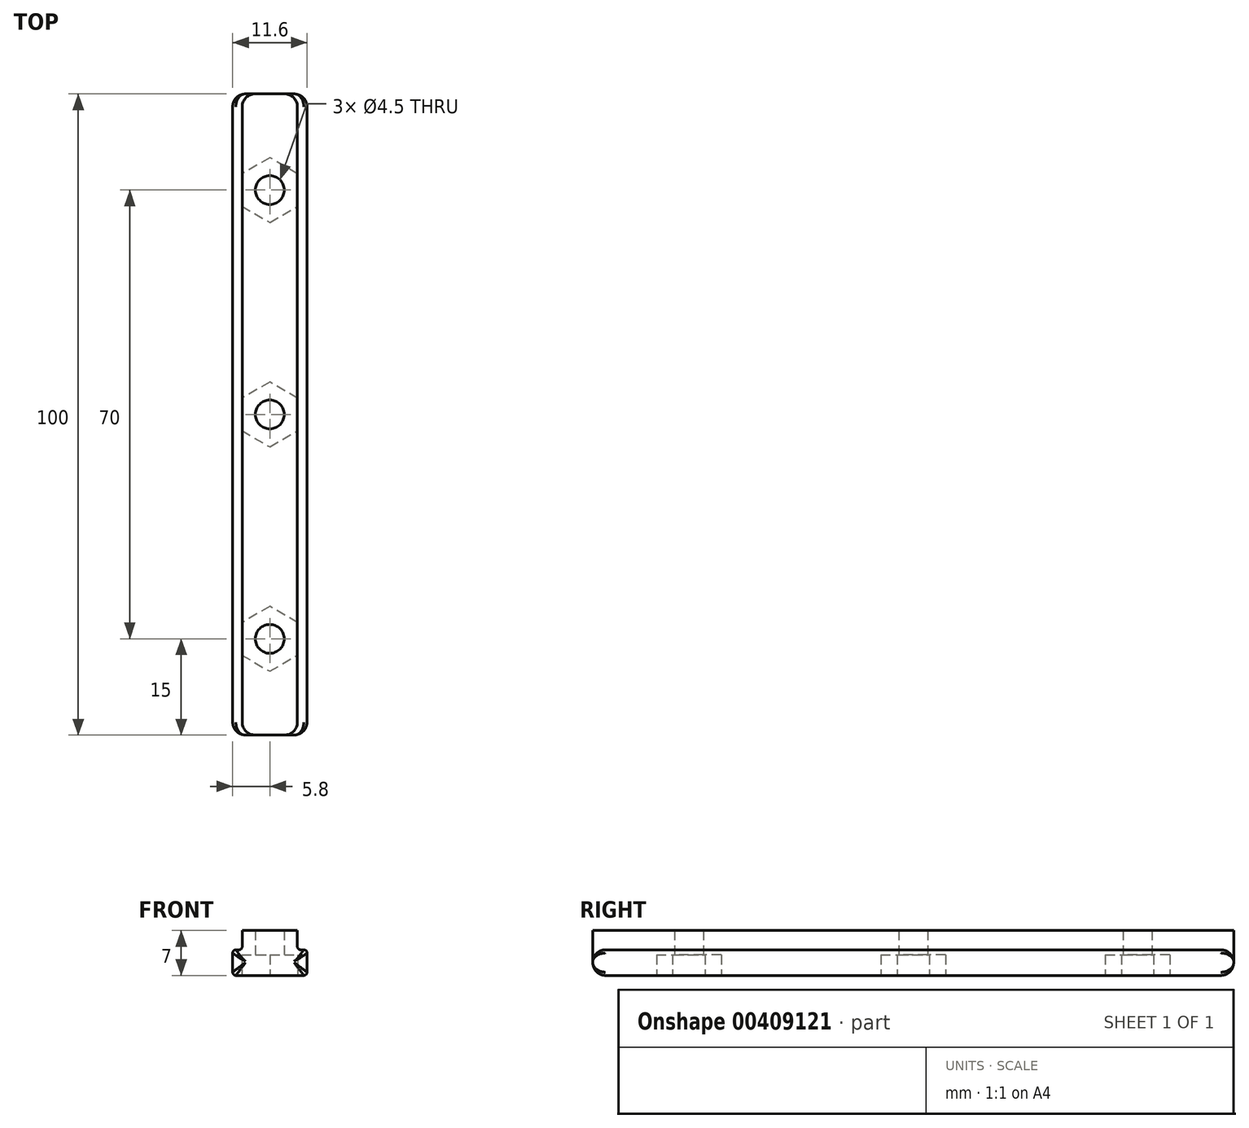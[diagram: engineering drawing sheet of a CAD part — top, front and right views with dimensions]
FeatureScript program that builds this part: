
annotation { "Feature Type Name" : "Feature", "Feature Type Description" : "" }
export const myFeature = defineFeature(function(context is Context, id is Id, definition is map)
    precondition{}
    {
        {
            var Q0;
            Q0=qCreatedBy(makeId("Front.planeOp"),FACE);
            var sketch = newSketch(context, id + "F0", { "sketchPlane" : qUnion([Q0])});
            skLineSegment(sketch, "E0", {"start": v(0, 0) * mm, "end": v(5.8, 0) * mm});
            skLineSegment(sketch, "E1", {"start": v(5.8, 0) * mm, "end": v(5.8, 4) * mm});
            skLineSegment(sketch, "E2", {"start": v(5.8, 4) * mm, "end": v(4.3, 4) * mm});
            skLineSegment(sketch, "E3", {"start": v(4.3, 4) * mm, "end": v(4.3, 7) * mm});
            skLineSegment(sketch, "E4", {"start": v(4.3, 7) * mm, "end": v(0, 7) * mm});
            skLineSegment(sketch, "E5", {"start": v(0, 0) * mm, "end": v(-5.8, 0) * mm});
            skLineSegment(sketch, "E6", {"start": v(-5.8, 0) * mm, "end": v(-5.8, 4) * mm});
            skLineSegment(sketch, "E7", {"start": v(-5.8, 4) * mm, "end": v(-4.3, 4) * mm});
            skLineSegment(sketch, "E8", {"start": v(-4.3, 4) * mm, "end": v(-4.3, 7) * mm});
            skLineSegment(sketch, "E9", {"start": v(-4.3, 7) * mm, "end": v(0, 7) * mm});
            skSolve(sketch);
        }
        {
            var Q0;
            Q0=makeQuery(id+"F0.imprint","IMPRINT",FACE,{"disambiguationData":[TD([[makeQuery(id+"F0.imprint","IMPRINT",EDGE,{"derivedFrom":sQuery(id+"F0.wireOp",EDGE,"E0")}),1.0]])]});
            extrude(context, id + "F1", {"entities" : qUnion([Q0]), "oppositeDirection" : true, "depth" : 100 * mm, "symmetric" : true});
        }
        {
            var Q0;
            Q0=makeQuery(id+"F1.opExtrude","SWEPT_FACE",FACE,{"disambiguationData":[OSD([sQuery(id+"F0.wireOp",EDGE,"E0"),sQuery(id+"F0.wireOp",EDGE,"E5")])]});
            var sketch = newSketch(context, id + "F2", { "sketchPlane" : qUnion([Q0])});
            skLineSegment(sketch, "E10", {"start": v(0, 54.75) * mm, "end": v(0, -56.35) * mm, "construction": true});
            skLineSegment(sketch, "E11", {"start": v(-11.08, 35) * mm, "end": v(14.13, 35) * mm, "construction": true});
            skLineSegment(sketch, "E12", {"start": v(-13, -35) * mm, "end": v(14.61, -35) * mm, "construction": true});
            skPoint(sketch, "E13", {"position": v(0, 35) * mm});
            skPoint(sketch, "E14", {"position": v(0, -35) * mm});
            skPoint(sketch, "E15", {"position": v(0, 0) * mm});
            skSolve(sketch);
        }
        {
            var Q0;
            Q0=sQuery(id+"F2.wireOp",VERTEX,"E13");
            var Q1;
            Q1=sQuery(id+"F2.wireOp",VERTEX,"E15");
            var Q2;
            Q2=sQuery(id+"F2.wireOp",VERTEX,"E14");
            var Q3;
            Q3=makeQuery(id+"F1.opExtrude","SWEPT_BODY",BODY,{"disambiguationData":[OSD([sQuery(id+"F0.wireOp",EDGE,"E0"),sQuery(id+"F0.wireOp",EDGE,"E1"),sQuery(id+"F0.wireOp",EDGE,"E2"),sQuery(id+"F0.wireOp",EDGE,"E3"),sQuery(id+"F0.wireOp",EDGE,"E4"),sQuery(id+"F0.wireOp",EDGE,"E5"),sQuery(id+"F0.wireOp",EDGE,"E6"),sQuery(id+"F0.wireOp",EDGE,"E7"),sQuery(id+"F0.wireOp",EDGE,"E8"),sQuery(id+"F0.wireOp",EDGE,"E9")])]});
            hole(context, id + "F3", {"style" : HoleStyle.SIMPLE, "endStyle" : HoleEndStyle.THROUGH, "standardTappedOrClearance" : lookupTablePath({ "standard" : "ANSI", "fit" : "Normal (ASME)", "size" : "#8", "type" : "Clearance" }), "standardBlindInLast" : lookupTablePath({ "fit" : "Free", "standard" : "ANSI", "size" : "#8", "type" : "Clearance" }), "holeDiameter" : 4.5 * mm, "isTappedThrough" : true, "tappedDepth" : 12 * mm, "tapClearance" : 3, "locations" : qUnion([Q0, Q1, Q2]), "scope" : qUnion([Q3])});
        }
        {
            var Q0;
            Q0=makeQuery(id+"F1.opExtrude","SWEPT_EDGE",EDGE,{"disambiguationData":[OSD([sQuery(id+"F0.wireOp",EDGE,"E2"),sQuery(id+"F0.wireOp",EDGE,"E3")])]});
            var Q1;
            Q1=makeQuery(id+"F1.opExtrude","SWEPT_EDGE",EDGE,{"disambiguationData":[OSD([sQuery(id+"F0.wireOp",EDGE,"E1"),sQuery(id+"F0.wireOp",EDGE,"E2")])]});
            var Q2;
            Q2=makeQuery(id+"F1.opExtrude","SWEPT_EDGE",EDGE,{"disambiguationData":[OSD([sQuery(id+"F0.wireOp",EDGE,"E0"),sQuery(id+"F0.wireOp",EDGE,"E1")])]});
            var Q3;
            Q3=makeQuery(id+"F1.opExtrude","SWEPT_EDGE",EDGE,{"disambiguationData":[OSD([sQuery(id+"F0.wireOp",EDGE,"E5"),sQuery(id+"F0.wireOp",EDGE,"E6")])]});
            var Q4;
            Q4=makeQuery(id+"F1.opExtrude","SWEPT_EDGE",EDGE,{"disambiguationData":[OSD([sQuery(id+"F0.wireOp",EDGE,"E6"),sQuery(id+"F0.wireOp",EDGE,"E7")])]});
            var Q5;
            Q5=makeQuery(id+"F1.opExtrude","SWEPT_EDGE",EDGE,{"disambiguationData":[OSD([sQuery(id+"F0.wireOp",EDGE,"E7"),sQuery(id+"F0.wireOp",EDGE,"E8")])]});
            fillet(context, id + "F4", {"entities" : qUnion([Q0, Q1, Q2, Q3, Q4, Q5]), "radius" : 0.5 * mm, "tangentPropagation" : true, "allowEdgeOverflow" : false});
        }
        {
            var Q0;
            Q0=makeQuery(id+"F1.opExtrude","CAP_EDGE",EDGE,{"disambiguationData":[OSD([sQuery(id+"F0.wireOp",EDGE,"E6")])],"isStart":true});
            var Q1;
            Q1=makeQuery(id+"F1.opExtrude","CAP_EDGE",EDGE,{"disambiguationData":[OSD([sQuery(id+"F0.wireOp",EDGE,"E0"),sQuery(id+"F0.wireOp",EDGE,"E5")])],"isStart":true});
            var Q2;
            Q2=makeQuery(id+"F1.opExtrude","CAP_EDGE",EDGE,{"disambiguationData":[OSD([sQuery(id+"F0.wireOp",EDGE,"E1")])],"isStart":true});
            var Q3;
            Q3=makeQuery(id+"F1.opExtrude","CAP_EDGE",EDGE,{"disambiguationData":[OSD([sQuery(id+"F0.wireOp",EDGE,"E0"),sQuery(id+"F0.wireOp",EDGE,"E5")])],"isStart":false});
            var Q4;
            Q4=makeQuery(id+"F1.opExtrude","CAP_EDGE",EDGE,{"disambiguationData":[OSD([sQuery(id+"F0.wireOp",EDGE,"E1")])],"isStart":false});
            fillet(context, id + "F5", {"entities" : qUnion([Q0, Q1, Q2, Q3, Q4]), "radius" : 2 * mm, "tangentPropagation" : true, "allowEdgeOverflow" : false});
        }
        {
            var Q0;
            Q0=makeQuery(id+"F1.opExtrude","SWEPT_FACE",FACE,{"disambiguationData":[OSD([sQuery(id+"F0.wireOp",EDGE,"E0"),sQuery(id+"F0.wireOp",EDGE,"E5")])]});
            var sketch = newSketch(context, id + "F6", { "sketchPlane" : qUnion([Q0])});
            skLineSegment(sketch, "E16.0", {"start": v(4.38, 2.53) * mm, "end": v(4.38, -2.53) * mm});
            skLineSegment(sketch, "E16.1", {"start": v(4.38, -2.53) * mm, "end": v(0, -5.05) * mm});
            skLineSegment(sketch, "E16.2", {"start": v(0, -5.05) * mm, "end": v(-4.38, -2.53) * mm});
            skLineSegment(sketch, "E16.3", {"start": v(-4.38, -2.53) * mm, "end": v(-4.38, 2.53) * mm});
            skLineSegment(sketch, "E16.4", {"start": v(-4.38, 2.53) * mm, "end": v(0, 5.05) * mm});
            skLineSegment(sketch, "E16.5", {"start": v(0, 5.05) * mm, "end": v(4.38, 2.53) * mm});
            skPoint(sketch, "E16.0.midPoint", {"position": v(4.38, 0) * mm});
            skLineSegment(sketch, "E17.0", {"start": v(4.38, -32.47) * mm, "end": v(4.38, -37.53) * mm});
            skLineSegment(sketch, "E17.1", {"start": v(4.38, -37.53) * mm, "end": v(0, -40.05) * mm});
            skLineSegment(sketch, "E17.2", {"start": v(0, -40.05) * mm, "end": v(-4.38, -37.53) * mm});
            skLineSegment(sketch, "E17.3", {"start": v(-4.38, -37.53) * mm, "end": v(-4.38, -32.47) * mm});
            skLineSegment(sketch, "E17.4", {"start": v(-4.38, -32.47) * mm, "end": v(0, -29.95) * mm});
            skLineSegment(sketch, "E17.5", {"start": v(0, -29.95) * mm, "end": v(4.37, -32.47) * mm});
            skPoint(sketch, "E17.0.midPoint", {"position": v(4.38, -35) * mm});
            skLineSegment(sketch, "E18.0", {"start": v(4.38, 37.53) * mm, "end": v(4.38, 32.47) * mm});
            skLineSegment(sketch, "E18.1", {"start": v(4.38, 32.47) * mm, "end": v(0, 29.95) * mm});
            skLineSegment(sketch, "E18.2", {"start": v(0, 29.95) * mm, "end": v(-4.38, 32.47) * mm});
            skLineSegment(sketch, "E18.3", {"start": v(-4.38, 32.47) * mm, "end": v(-4.38, 37.53) * mm});
            skLineSegment(sketch, "E18.4", {"start": v(-4.38, 37.53) * mm, "end": v(0, 40.05) * mm});
            skLineSegment(sketch, "E18.5", {"start": v(0, 40.05) * mm, "end": v(4.38, 37.53) * mm});
            skPoint(sketch, "E18.0.midPoint", {"position": v(4.38, 35) * mm});
            skSolve(sketch);
        }
        {
            var Q0;
            Q0=makeQuery(id+"F6.imprint","IMPRINT",FACE,{"disambiguationData":[TD([[makeQuery(id+"F6.imprint","IMPRINT",EDGE,{"derivedFrom":sQuery(id+"F6.wireOp",EDGE,"E18.0")}),-1.0]])]});
            var Q1;
            Q1=makeQuery(id+"F6.imprint","IMPRINT",FACE,{"disambiguationData":[TD([[makeQuery(id+"F6.imprint","IMPRINT",EDGE,{"derivedFrom":sQuery(id+"F6.wireOp",EDGE,"E16.0")}),-1.0]])]});
            var Q2;
            Q2=makeQuery(id+"F6.imprint","IMPRINT",FACE,{"disambiguationData":[TD([[makeQuery(id+"F6.imprint","IMPRINT",EDGE,{"derivedFrom":sQuery(id+"F6.wireOp",EDGE,"E17.0")}),-1.0]])]});
            extrude(context, id + "F7", {"entities" : qUnion([Q0, Q1, Q2]), "operationType" : NewBodyOperationType.REMOVE, "oppositeDirection" : true, "depth" : 3.2 * mm, "offsetDistance" : 25 * mm});
        }
    });
